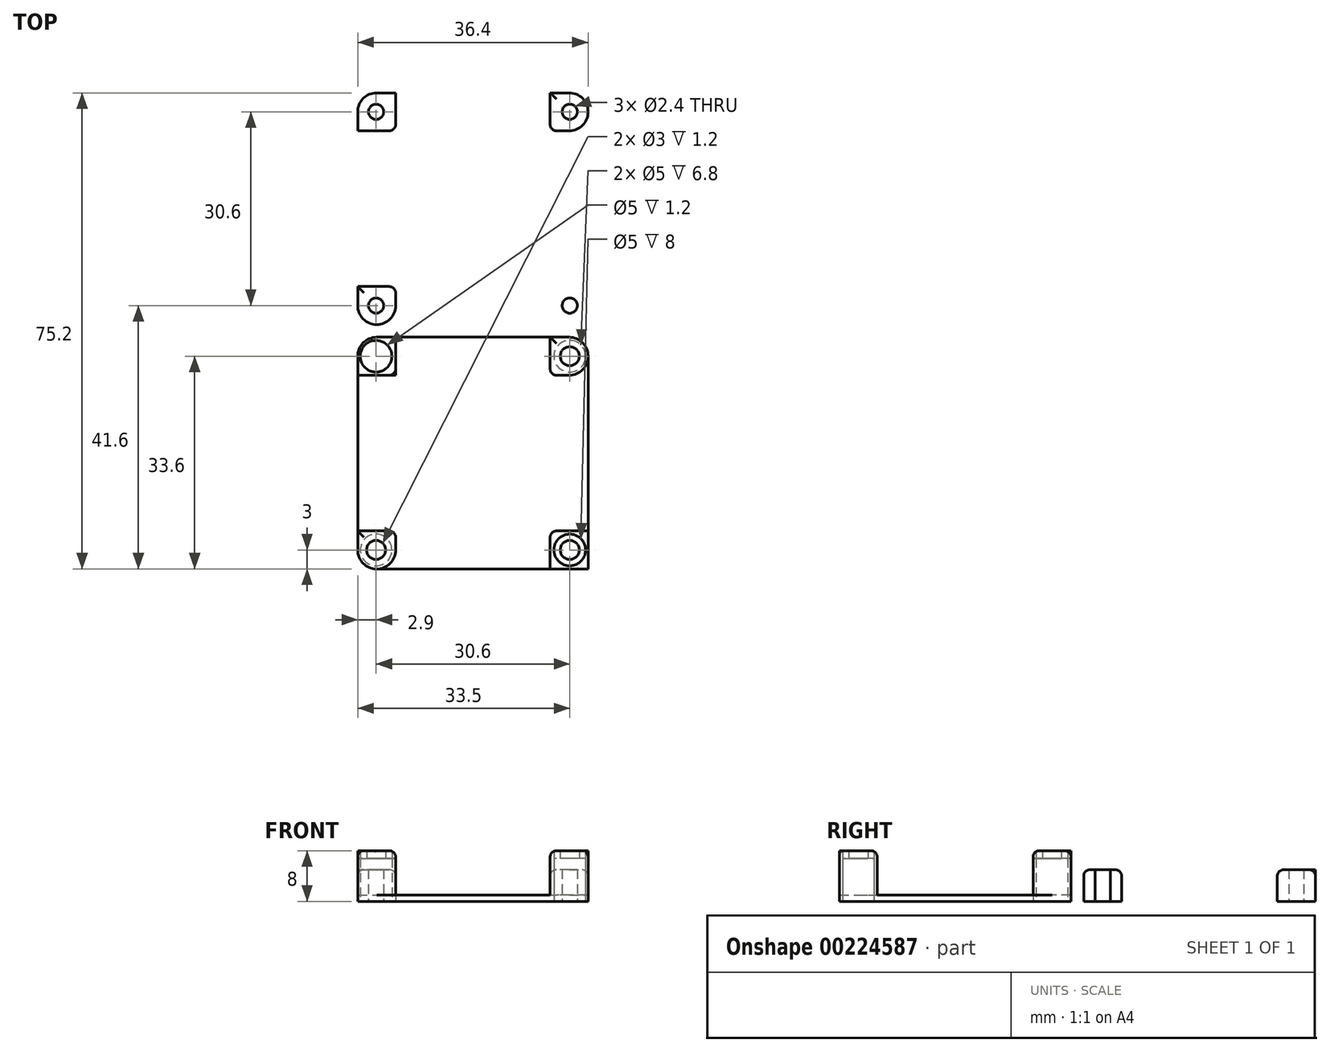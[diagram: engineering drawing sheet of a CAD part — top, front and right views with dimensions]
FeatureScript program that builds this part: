
annotation { "Feature Type Name" : "Feature", "Feature Type Description" : "" }
export const myFeature = defineFeature(function(context is Context, id is Id, definition is map)
    precondition{}
    {
        {
            var Q0;
            Q0=qCreatedBy(makeId("Top.planeOp"),FACE);
            var sketch = newSketch(context, id + "F0", { "sketchPlane" : qUnion([Q0])});
            skLineSegment(sketch, "E0.bottom", {"start": v(18.2, -18.3) * mm, "end": v(-18.2, -18.3) * mm});
            skLineSegment(sketch, "E0.top", {"start": v(18.2, 18.3) * mm, "end": v(-18.2, 18.3) * mm});
            skLineSegment(sketch, "E0.left", {"start": v(18.2, -18.3) * mm, "end": v(18.2, 18.3) * mm});
            skLineSegment(sketch, "E0.right", {"start": v(-18.2, -18.3) * mm, "end": v(-18.2, 18.3) * mm});
            skPoint(sketch, "E0.middle", {"position": v(0, 0) * mm});
            skLineSegment(sketch, "E1.bottom", {"start": v(15.3, -15.3) * mm, "end": v(-15.3, -15.3) * mm, "construction": true});
            skLineSegment(sketch, "E1.top", {"start": v(15.3, 15.3) * mm, "end": v(-15.3, 15.3) * mm, "construction": true});
            skLineSegment(sketch, "E1.left", {"start": v(15.3, -15.3) * mm, "end": v(15.3, 15.3) * mm, "construction": true});
            skLineSegment(sketch, "E1.right", {"start": v(-15.3, -15.3) * mm, "end": v(-15.3, 15.3) * mm, "construction": true});
            skCircle(sketch, "E2", {"center": v(15.3, 15.3) * mm, "radius": 1.2 * mm});
            skLineSegment(sketch, "E3.bottom", {"start": v(18.2, 18.3) * mm, "end": v(12.2, 18.3) * mm});
            skLineSegment(sketch, "E3.top", {"start": v(18.2, 12.3) * mm, "end": v(12.2, 12.3) * mm});
            skLineSegment(sketch, "E3.left", {"start": v(18.2, 18.3) * mm, "end": v(18.2, 12.3) * mm});
            skLineSegment(sketch, "E3.right", {"start": v(12.2, 18.3) * mm, "end": v(12.2, 12.3) * mm});
            skPoint(sketch, "E4.center", {"position": v(0, -0.6) * mm});
            skLineSegment(sketch, "E5.MirrorCS", {"start": v(-18.2, 12.3) * mm, "end": v(-12.2, 12.3) * mm});
            skLineSegment(sketch, "E6.MirrorCS", {"start": v(-12.2, 18.3) * mm, "end": v(-12.2, 12.3) * mm});
            skCircle(sketch, "E7.MirrorC", {"center": v(-15.3, 15.3) * mm, "radius": 1.2 * mm});
            skCircle(sketch, "E8.MirrorC", {"center": v(15.3, -15.3) * mm, "radius": 1.2 * mm});
            skLineSegment(sketch, "E9.MirrorCS", {"start": v(12.2, -18.3) * mm, "end": v(12.2, -12.3) * mm});
            skLineSegment(sketch, "E10.MirrorCS", {"start": v(18.2, -12.3) * mm, "end": v(12.2, -12.3) * mm});
            skCircle(sketch, "E11.MirrorC", {"center": v(-15.3, -15.3) * mm, "radius": 1.2 * mm});
            skLineSegment(sketch, "E12.MirrorCS", {"start": v(-18.2, -12.3) * mm, "end": v(-12.2, -12.3) * mm});
            skLineSegment(sketch, "E13.MirrorCS", {"start": v(-12.2, -18.3) * mm, "end": v(-12.2, -12.3) * mm});
            skLineSegment(sketch, "E14", {"start": v(-5.92, -19.3) * mm, "end": v(6.77, -19.3) * mm, "construction": true});
            skPoint(sketch, "E15.MirrorP", {"position": v(0, -38.6) * mm});
            skPoint(sketch, "E16.MirrorP", {"position": v(0, -38) * mm});
            skLineSegment(sketch, "E17.MirrorCS", {"start": v(18.2, -50.9) * mm, "end": v(12.2, -50.9) * mm});
            skLineSegment(sketch, "E18.MirrorCS", {"start": v(12.2, -56.9) * mm, "end": v(12.2, -50.9) * mm});
            skLineSegment(sketch, "E19.MirrorCS", {"start": v(15.3, -23.3) * mm, "end": v(15.3, -53.9) * mm, "construction": true});
            skLineSegment(sketch, "E20.MirrorCS", {"start": v(18.2, -56.9) * mm, "end": v(18.2, -50.9) * mm});
            skLineSegment(sketch, "E21.MirrorCS", {"start": v(12.2, -20.3) * mm, "end": v(12.2, -26.3) * mm});
            skLineSegment(sketch, "E22.MirrorCS", {"start": v(15.3, -23.3) * mm, "end": v(-15.3, -23.3) * mm, "construction": true});
            skLineSegment(sketch, "E23.MirrorCS", {"start": v(-18.2, -50.9) * mm, "end": v(-12.2, -50.9) * mm});
            skLineSegment(sketch, "E24.MirrorCS", {"start": v(-12.2, -56.9) * mm, "end": v(-12.2, -50.9) * mm});
            skLineSegment(sketch, "E25.MirrorCS", {"start": v(-18.2, -26.3) * mm, "end": v(-12.2, -26.3) * mm});
            skLineSegment(sketch, "E26.MirrorCS", {"start": v(15.3, -53.9) * mm, "end": v(-15.3, -53.9) * mm, "construction": true});
            skLineSegment(sketch, "E27.MirrorCS", {"start": v(-15.3, -23.3) * mm, "end": v(-15.3, -53.9) * mm, "construction": true});
            skLineSegment(sketch, "E28.MirrorCS", {"start": v(18.2, -20.3) * mm, "end": v(18.2, -56.9) * mm});
            skLineSegment(sketch, "E29.MirrorCS", {"start": v(18.2, -56.9) * mm, "end": v(12.2, -56.9) * mm});
            skLineSegment(sketch, "E30.MirrorCS", {"start": v(18.2, -56.9) * mm, "end": v(-18.2, -56.9) * mm});
            skLineSegment(sketch, "E31.MirrorCS", {"start": v(-18.2, -20.3) * mm, "end": v(-18.2, -56.9) * mm});
            skLineSegment(sketch, "E32.MirrorCS", {"start": v(18.2, -20.3) * mm, "end": v(-18.2, -20.3) * mm});
            skLineSegment(sketch, "E33.MirrorCS", {"start": v(18.2, -26.3) * mm, "end": v(12.2, -26.3) * mm});
            skLineSegment(sketch, "E34.MirrorCS", {"start": v(-12.2, -20.3) * mm, "end": v(-12.2, -26.3) * mm});
            skCircle(sketch, "E35", {"center": v(15.3, -23.3) * mm, "radius": 2.5 * mm});
            skCircle(sketch, "E36", {"center": v(15.3, -23.3) * mm, "radius": 1.5 * mm});
            skCircle(sketch, "E37.MirrorC", {"center": v(-15.3, -23.3) * mm, "radius": 2.5 * mm});
            skCircle(sketch, "E38.MirrorC", {"center": v(-15.3, -23.3) * mm, "radius": 1.5 * mm});
            skLineSegment(sketch, "E39", {"start": v(0, -38.6) * mm, "end": v(5.34, -38.6) * mm, "construction": true});
            skCircle(sketch, "E40.MirrorC", {"center": v(15.3, -53.9) * mm, "radius": 1.5 * mm});
            skCircle(sketch, "E41.MirrorC", {"center": v(15.3, -53.9) * mm, "radius": 2.5 * mm});
            skCircle(sketch, "E42.MirrorC", {"center": v(-15.3, -53.9) * mm, "radius": 1.5 * mm});
            skCircle(sketch, "E43.MirrorC", {"center": v(-15.3, -53.9) * mm, "radius": 2.5 * mm});
            skSolve(sketch);
        }
        {
            var Q0;
            {var subQ1=sQuery(id+"F0.wireOp",EDGE,"E5.MirrorCS");Q0=makeQuery(id+"F0.imprint","IMPRINT",FACE,{"disambiguationData":[TD([[makeQuery(id+"F0.imprint","IMPRINT",EDGE,{"derivedFrom":subQ1}),-1.0]])]});}
            var Q1;
            {var subQ6=sQuery(id+"F0.wireOp",EDGE,"E18.MirrorCS");Q1=makeQuery(id+"F0.imprint","IMPRINT",FACE,{"disambiguationData":[TD([[makeQuery(id+"F0.imprint","IMPRINT",EDGE,{"derivedFrom":subQ6}),1.0]])]});}
            extrude(context, id + "F1", {"entities" : qUnion([Q0, Q1]), "depth" : 1 * mm});
        }
        {
            var Q0;
            Q0=makeQuery(id+"F0.imprint","IMPRINT",FACE,{"disambiguationData":[TD([[makeQuery(id+"F0.imprint","IMPRINT",EDGE,{"derivedFrom":sQuery(id+"F0.wireOp",EDGE,"E11.MirrorC")}),-1.0]])]});
            var Q1;
            Q1=makeQuery(id+"F0.imprint","IMPRINT",FACE,{"disambiguationData":[TD([[makeQuery(id+"F0.imprint","IMPRINT",EDGE,{"derivedFrom":sQuery(id+"F0.wireOp",EDGE,"E8.MirrorC")}),1.0]])]});
            var Q2;
            {var subQ1=sQuery(id+"F0.wireOp",EDGE,"E5.MirrorCS");Q2=makeQuery(id+"F0.imprint","IMPRINT",FACE,{"disambiguationData":[TD([[makeQuery(id+"F0.imprint","IMPRINT",EDGE,{"derivedFrom":subQ1}),1.0]])]});}
            var Q3;
            Q3=makeQuery(id+"F0.imprint","IMPRINT",FACE,{"disambiguationData":[TD([[makeQuery(id+"F0.imprint","IMPRINT",EDGE,{"derivedFrom":sQuery(id+"F0.wireOp",EDGE,"E2")}),-1.0]])]});
            extrude(context, id + "F2", {"entities" : qUnion([Q0, Q1, Q2, Q3]), "operationType" : NewBodyOperationType.ADD, "depth" : 5 * mm});
        }
        {
            var Q0;
            {var subQ4=sQuery(id+"F0.wireOp",EDGE,"E25.MirrorCS");Q0=makeQuery(id+"F0.imprint","IMPRINT",FACE,{"disambiguationData":[TD([[makeQuery(id+"F0.imprint","IMPRINT",EDGE,{"derivedFrom":subQ4}),1.0]])]});}
            var Q1;
            Q1=makeQuery(id+"F0.imprint","IMPRINT",FACE,{"disambiguationData":[TD([[makeQuery(id+"F0.imprint","IMPRINT",EDGE,{"derivedFrom":sQuery(id+"F0.wireOp",EDGE,"E37.MirrorC")}),-1.0]])]});
            var Q2;
            {var subQ1=sQuery(id+"F0.wireOp",EDGE,"E21.MirrorCS");Q2=makeQuery(id+"F0.imprint","IMPRINT",FACE,{"disambiguationData":[TD([[makeQuery(id+"F0.imprint","IMPRINT",EDGE,{"derivedFrom":subQ1}),1.0]])]});}
            var Q3;
            Q3=makeQuery(id+"F0.imprint","IMPRINT",FACE,{"disambiguationData":[TD([[makeQuery(id+"F0.imprint","IMPRINT",EDGE,{"derivedFrom":sQuery(id+"F0.wireOp",EDGE,"E35")}),1.0]])]});
            var Q4;
            Q4=makeQuery(id+"F0.imprint","IMPRINT",FACE,{"disambiguationData":[TD([[makeQuery(id+"F0.imprint","IMPRINT",EDGE,{"derivedFrom":sQuery(id+"F0.wireOp",EDGE,"E40.MirrorC")}),1.0]])]});
            var Q5;
            {var subQ2=sQuery(id+"F0.wireOp",EDGE,"E18.MirrorCS");Q5=makeQuery(id+"F0.imprint","IMPRINT",FACE,{"disambiguationData":[TD([[makeQuery(id+"F0.imprint","IMPRINT",EDGE,{"derivedFrom":subQ2}),-1.0]])]});}
            var Q6;
            {var subQ1=sQuery(id+"F0.wireOp",EDGE,"E23.MirrorCS");Q6=makeQuery(id+"F0.imprint","IMPRINT",FACE,{"disambiguationData":[TD([[makeQuery(id+"F0.imprint","IMPRINT",EDGE,{"derivedFrom":subQ1}),-1.0]])]});}
            var Q7;
            Q7=makeQuery(id+"F0.imprint","IMPRINT",FACE,{"disambiguationData":[TD([[makeQuery(id+"F0.imprint","IMPRINT",EDGE,{"derivedFrom":sQuery(id+"F0.wireOp",EDGE,"E42.MirrorC")}),-1.0]])]});
            extrude(context, id + "F3", {"entities" : qUnion([Q0, Q1, Q2, Q3, Q4, Q5, Q6, Q7]), "operationType" : NewBodyOperationType.ADD, "depth" : 8 * mm});
        }
        {
            var Q0;
            Q0=makeQuery(id+"F0.imprint","IMPRINT",FACE,{"disambiguationData":[TD([[makeQuery(id+"F0.imprint","IMPRINT",EDGE,{"derivedFrom":sQuery(id+"F0.wireOp",EDGE,"E37.MirrorC")}),-1.0]])]});
            var Q1;
            Q1=makeQuery(id+"F0.imprint","IMPRINT",FACE,{"disambiguationData":[TD([[makeQuery(id+"F0.imprint","IMPRINT",EDGE,{"derivedFrom":sQuery(id+"F0.wireOp",EDGE,"E35")}),1.0]])]});
            var Q2;
            Q2=makeQuery(id+"F0.imprint","IMPRINT",FACE,{"disambiguationData":[TD([[makeQuery(id+"F0.imprint","IMPRINT",EDGE,{"derivedFrom":sQuery(id+"F0.wireOp",EDGE,"E40.MirrorC")}),1.0]])]});
            var Q3;
            Q3=makeQuery(id+"F0.imprint","IMPRINT",FACE,{"disambiguationData":[TD([[makeQuery(id+"F0.imprint","IMPRINT",EDGE,{"derivedFrom":sQuery(id+"F0.wireOp",EDGE,"E42.MirrorC")}),-1.0]])]});
            extrude(context, id + "F4", {"entities" : qUnion([Q0, Q1, Q2, Q3]), "operationType" : NewBodyOperationType.REMOVE, "depth" : 6.8 * mm});
        }
        {
            var Q0;
            Q0=makeQuery(id+"F2.opExtrude","SWEPT_EDGE",EDGE,{"disambiguationData":[OSD([sQuery(id+"F0.wireOp",EDGE,"E0.bottom"),sQuery(id+"F0.wireOp",EDGE,"E0.right")])]});
            var Q1;
            Q1=makeQuery(id+"F3.opExtrude","SWEPT_EDGE",EDGE,{"disambiguationData":[OSD([sQuery(id+"F0.wireOp",EDGE,"E31.MirrorCS"),sQuery(id+"F0.wireOp",EDGE,"E32.MirrorCS")])]});
            var Q2;
            Q2=makeQuery(id+"F3.opExtrude","SWEPT_EDGE",EDGE,{"disambiguationData":[OSD([sQuery(id+"F0.wireOp",EDGE,"E30.MirrorCS"),sQuery(id+"F0.wireOp",EDGE,"E31.MirrorCS")])]});
            var Q3;
            Q3=makeQuery(id+"F2.opExtrude","SWEPT_EDGE",EDGE,{"disambiguationData":[OSD([sQuery(id+"F0.wireOp",EDGE,"E0.top"),sQuery(id+"F0.wireOp",EDGE,"E0.right")])]});
            var Q4;
            Q4=makeQuery(id+"F3.opExtrude","SWEPT_EDGE",EDGE,{"disambiguationData":[OSD([sQuery(id+"F0.wireOp",EDGE,"E28.MirrorCS"),sQuery(id+"F0.wireOp",EDGE,"E30.MirrorCS")])]});
            var Q5;
            Q5=makeQuery(id+"F3.opExtrude","SWEPT_EDGE",EDGE,{"disambiguationData":[OSD([sQuery(id+"F0.wireOp",EDGE,"E28.MirrorCS"),sQuery(id+"F0.wireOp",EDGE,"E32.MirrorCS")])]});
            var Q6;
            Q6=makeQuery(id+"F2.opExtrude","SWEPT_EDGE",EDGE,{"disambiguationData":[OSD([sQuery(id+"F0.wireOp",EDGE,"E0.bottom"),sQuery(id+"F0.wireOp",EDGE,"E0.left")])]});
            var Q7;
            Q7=makeQuery(id+"F2.opExtrude","SWEPT_EDGE",EDGE,{"disambiguationData":[OSD([sQuery(id+"F0.wireOp",EDGE,"E3.bottom"),sQuery(id+"F0.wireOp",EDGE,"E3.left")])]});
            fillet(context, id + "F5", {"entities" : qUnion([Q0, Q1, Q2, Q3, Q4, Q5, Q6, Q7]), "radius" : 3 * mm, "tangentPropagation" : true, "allowEdgeOverflow" : false});
        }
        {
            var Q0;
            Q0=makeQuery(id+"F3.opExtrude","CAP_EDGE",EDGE,{"disambiguationData":[OSD([sQuery(id+"F0.wireOp",EDGE,"E17.MirrorCS")])],"isStart":false});
            var Q1;
            Q1=makeQuery(id+"F3.opExtrude","CAP_EDGE",EDGE,{"disambiguationData":[OSD([sQuery(id+"F0.wireOp",EDGE,"E24.MirrorCS")])],"isStart":false});
            var Q2;
            Q2=makeQuery(id+"F3.opExtrude","CAP_EDGE",EDGE,{"disambiguationData":[OSD([sQuery(id+"F0.wireOp",EDGE,"E23.MirrorCS")])],"isStart":false});
            var Q3;
            Q3=makeQuery(id+"F3.opExtrude","SWEPT_EDGE",EDGE,{"disambiguationData":[OSD([sQuery(id+"F0.wireOp",EDGE,"E23.MirrorCS"),sQuery(id+"F0.wireOp",EDGE,"E24.MirrorCS")])]});
            var Q4;
            Q4=makeQuery(id+"F3.opExtrude","SWEPT_EDGE",EDGE,{"disambiguationData":[OSD([sQuery(id+"F0.wireOp",EDGE,"E18.MirrorCS"),sQuery(id+"F0.wireOp",EDGE,"E17.MirrorCS")])]});
            var Q5;
            Q5=makeQuery(id+"F3.opExtrude","CAP_EDGE",EDGE,{"disambiguationData":[OSD([sQuery(id+"F0.wireOp",EDGE,"E18.MirrorCS")])],"isStart":false});
            var Q6;
            Q6=makeQuery(id+"F3.opExtrude","CAP_EDGE",EDGE,{"disambiguationData":[OSD([sQuery(id+"F0.wireOp",EDGE,"E21.MirrorCS")])],"isStart":false});
            var Q7;
            Q7=makeQuery(id+"F3.opExtrude","CAP_EDGE",EDGE,{"disambiguationData":[OSD([sQuery(id+"F0.wireOp",EDGE,"E33.MirrorCS")])],"isStart":false});
            var Q8;
            Q8=makeQuery(id+"F3.opExtrude","SWEPT_EDGE",EDGE,{"disambiguationData":[OSD([sQuery(id+"F0.wireOp",EDGE,"E21.MirrorCS"),sQuery(id+"F0.wireOp",EDGE,"E33.MirrorCS")])]});
            var Q9;
            Q9=makeQuery(id+"F3.opExtrude","CAP_EDGE",EDGE,{"disambiguationData":[OSD([sQuery(id+"F0.wireOp",EDGE,"E34.MirrorCS")])],"isStart":false});
            var Q10;
            Q10=makeQuery(id+"F3.opExtrude","CAP_EDGE",EDGE,{"disambiguationData":[OSD([sQuery(id+"F0.wireOp",EDGE,"E25.MirrorCS")])],"isStart":false});
            var Q11;
            Q11=makeQuery(id+"F3.opExtrude","SWEPT_EDGE",EDGE,{"disambiguationData":[OSD([sQuery(id+"F0.wireOp",EDGE,"E25.MirrorCS"),sQuery(id+"F0.wireOp",EDGE,"E34.MirrorCS")])]});
            var Q12;
            Q12=makeQuery(id+"F2.opExtrude","SWEPT_EDGE",EDGE,{"disambiguationData":[OSD([sQuery(id+"F0.wireOp",EDGE,"E12.MirrorCS"),sQuery(id+"F0.wireOp",EDGE,"E13.MirrorCS")])]});
            var Q13;
            Q13=makeQuery(id+"F2.opExtrude","CAP_EDGE",EDGE,{"disambiguationData":[OSD([sQuery(id+"F0.wireOp",EDGE,"E13.MirrorCS")])],"isStart":false});
            var Q14;
            Q14=makeQuery(id+"F2.opExtrude","CAP_EDGE",EDGE,{"disambiguationData":[OSD([sQuery(id+"F0.wireOp",EDGE,"E12.MirrorCS")])],"isStart":false});
            var Q15;
            Q15=makeQuery(id+"F2.opExtrude","CAP_EDGE",EDGE,{"disambiguationData":[OSD([sQuery(id+"F0.wireOp",EDGE,"E9.MirrorCS")])],"isStart":false});
            var Q16;
            Q16=makeQuery(id+"F2.opExtrude","CAP_EDGE",EDGE,{"disambiguationData":[OSD([sQuery(id+"F0.wireOp",EDGE,"E10.MirrorCS")])],"isStart":false});
            var Q17;
            Q17=makeQuery(id+"F2.opExtrude","SWEPT_EDGE",EDGE,{"disambiguationData":[OSD([sQuery(id+"F0.wireOp",EDGE,"E9.MirrorCS"),sQuery(id+"F0.wireOp",EDGE,"E10.MirrorCS")])]});
            var Q18;
            Q18=makeQuery(id+"F2.opExtrude","CAP_EDGE",EDGE,{"disambiguationData":[OSD([sQuery(id+"F0.wireOp",EDGE,"E3.top")])],"isStart":false});
            var Q19;
            Q19=makeQuery(id+"F2.opExtrude","CAP_EDGE",EDGE,{"disambiguationData":[OSD([sQuery(id+"F0.wireOp",EDGE,"E3.right")])],"isStart":false});
            var Q20;
            Q20=makeQuery(id+"F2.opExtrude","CAP_EDGE",EDGE,{"disambiguationData":[OSD([sQuery(id+"F0.wireOp",EDGE,"E6.MirrorCS")])],"isStart":false});
            var Q21;
            Q21=makeQuery(id+"F2.opExtrude","SWEPT_EDGE",EDGE,{"disambiguationData":[OSD([sQuery(id+"F0.wireOp",EDGE,"E5.MirrorCS"),sQuery(id+"F0.wireOp",EDGE,"E6.MirrorCS")])]});
            var Q22;
            Q22=makeQuery(id+"F2.opExtrude","CAP_EDGE",EDGE,{"disambiguationData":[OSD([sQuery(id+"F0.wireOp",EDGE,"E5.MirrorCS")])],"isStart":false});
            var Q23;
            Q23=makeQuery(id+"F2.opExtrude","SWEPT_EDGE",EDGE,{"disambiguationData":[OSD([sQuery(id+"F0.wireOp",EDGE,"E3.top"),sQuery(id+"F0.wireOp",EDGE,"E3.right")])]});
            fillet(context, id + "F6", {"entities" : qUnion([Q0, Q1, Q2, Q3, Q4, Q5, Q6, Q7, Q8, Q9, Q10, Q11, Q12, Q13, Q14, Q15, Q16, Q17, Q18, Q19, Q20, Q21, Q22, Q23]), "radius" : 1 * mm, "tangentPropagation" : true, "allowEdgeOverflow" : false});
        }
    });
